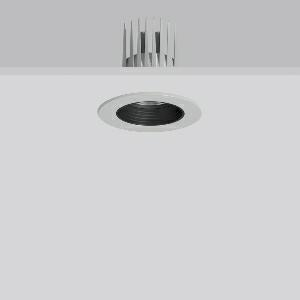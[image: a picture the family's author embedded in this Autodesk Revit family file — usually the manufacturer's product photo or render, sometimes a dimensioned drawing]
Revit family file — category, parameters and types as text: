
# Revit family: heledon_mini_e_901753_004_cf74
name_source: partatom
category: Lighting Fixtures
units: mm (PartAtom-declared; Revit-internal decimal feet)

## family parameters
Cut with Voids When Loaded = No
Host = Face
Light Source = No
Part Type = Normal
Room Calculation Point = No
Round Connector Dimension = Use Diameter
Shared = No

## types (1)
- HELEDON mini E (1 x LED Modul 930, 2850 lm, 3000)
    Apparent Load = 29 VA
    Approval mark = CE
    CIE Flux Codes = 98 100 100 100 100
    Color Rendering = 90
    Color Temperature = 3000
    Default Elevation = 1800 mm
    Description = Series: HELEDON mini
Round recessed downlight. Housing: die-cast aluminium, powder-coated. Black plastic ring and recessed LED to prevent glare from the side. Optical assembly with lens made of plastic (polycarbonate) for the best homogeneous light distribution - can be changed without tools. Best colour rendering index Ra>90. Suitable for Recessed ceiling mounting. Installation without tools thanks to spring fastening system. Including separate LED converter with connecting cable 600 mm.High quality converter without flickering and stroboscopic effect. Through-wiring box (5 pole) available as accessory. The following accessories can be mounted without use of tools: interchangeable lenses, decorative glasses, honeycomb louvre, clear and frosted diffusers, white interchangeable plastic ring. 
Colour: silver
Diameter: 124 mm
Height: 3 mm
Cut-out diameter: 114 mm
Recess height: 170 mm
Luminaire: recess height: 120 mm
Lamp: LED
Socket: without socket
Colour temperature: 3000K
Colour rendering index (CRI): 92
System power: 29 W
Rated luminous flux: 2850 lm
Luminous efficiency: 98 lm/W
Control gear: Regulated power supply
Protection class: II
Type of protection: IP 20
    Height = 0 mm  [stored 0 ft]
    Lamp = 1 x LED Modul 930
    Lamp Light Flux = 2850 lm
    Lamp count = 1
    Length = 124 mm  [stored 0.406824 ft]
    Lifetime = 50000 h
    Luminous efficacy = 98 lm/W
    Manufacturer = RZB
    ModVariant = No
    Model = 901753.004
    Mounting Place = Ceiling
    Mounting Type = Recessed
    Number of Poles = 1
    OnlyDefault = Yes
    Power Factor = 1
    Product Name = HELEDON mini E
    Product group = Recessed downlights
    ProductGroupID = 402
    Protection Class = Protection class II
    Protection Degree = IP 20
    RLX_Detail_Level = 1
    RLX_Emergency_Light_Flux = 0 lm
    RLX_Emergency_Type = 0
    RLX_Emergency_Type_DB = No
    RlxData = <blob elided: 125721 chars, md5=86bba1a9>
    Socket = socket
    Standby Power = 0 W
    System Light Flux = 2850 lm
    System Power = 29 W
    Type Comments = Product without accessories
    Type Image = 901656.004.jpg
    URL = http://relux.com
    VarID = ---
    Voltage = 230 V
    Voltage Range = 220-240 V
    Weight = 0.00 kg
    Width = 0 mm  [stored 0 ft]

note: [stored X ft] marks values corroborated as IEEE doubles in the binary element streams (Revit-internal decimal feet)

## geometry (parser evidence)
native form markers: Blend x4, Sweep x11
no freeform markers — native parametric forms only
